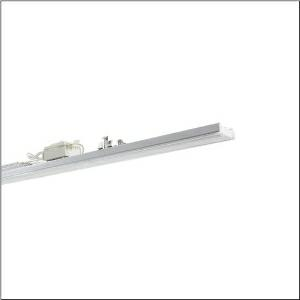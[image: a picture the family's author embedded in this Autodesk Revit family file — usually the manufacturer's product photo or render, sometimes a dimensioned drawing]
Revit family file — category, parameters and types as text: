
# Revit family: licross_r__11_recessed_ho_51tl1wdv4m2m_e1c2
name_source: partatom
category: Lighting Fixtures
units: mm (PartAtom-declared; Revit-internal decimal feet)

## family parameters
Cut with Voids When Loaded = No
Host = Face
Light Source = No
Part Type = Normal
Room Calculation Point = No
Round Connector Dimension = Use Diameter
Shared = No

## types (1)
- --- (1 x LED, 27420 lm, 150.5 W, 4000K)
    Apparent Load = 150 VA
    CIE Flux Codes = 73 94 99 100 100
    Color Rendering = 80
    Color Temperature = 4000K
    Default Elevation = 1800 mm
    Description = Licross® 11 Recessed HO, luminaire insert, of sheet steel, coil coated, white, length: 2.250mm, width: 66mm, height: 67mm, LED rated luminous flux: 27.420lm, light colour: 840, control gear: DALI 2, with plug, 5-pole, with phase selection, mains connection: 220..240V, AC, 50/60Hz, rated input power: 151W, internal wiring halogen-free, primary optical cover: cover, of PMMA, light emission: direct distribution, primary light characteristic: symmetric, protection rating (complete): IP40, insulation class (complete): insulation class I (protective earthing), certification: CE, ENEC, VDE, UKCA, protection symbol: D if used in an environment without relevant dust loads with corresponding accessories, impact resistance: IK06, permissible ambient temperature for indoor applications: -40..+35°C, corresponds to IFS (International Featured Standards) requirements for safety and quality in the food industry, reducing of maximum allowable ambient temperature of 5°C with ceiling mounting, LABS conformity tested according to VDMA 24364:2018-05, packaging unit: 1 piece
    Height = 58 mm
    Lamp = 1 x LED
    Lamp Light Flux = 27420 lm
    Lamp Power = 150.5 W
    Lamp count = 1
    Length = 2250 mm
    Luminous efficacy = 182 lm/W
    Manufacturer = Siteco
    ModVariant = No
    Model = 51TL1WDV4M2M
    Mounting Place = Ceiling
    Mounting Type = Pendant
    Number of Poles = 1
    OnlyDefault = Yes
    Power Factor = 1
    Product Name = Licross® 11 Recessed HO
    Product group = luminaire insert | ceiling pendant
    ProductGroupID = 902
    Protection Class = Protection class I
    Protection Degree = IP 40
    RLX_Detail_Level = 1
    RLX_Emergency_Light_Flux = 0 lm
    RLX_Emergency_Type = 0
    RLX_Emergency_Type_DB = No
    RlxData = <blob elided: 29653 chars, md5=4ee0cf90>
    Socket = socket
    Standby Power = 0 W
    System Light Flux = 27420 lm
    System Power = 150 W
    Type Comments = factory setting: luminous flux: 100 % | dim-lin: 254 | 690 mA
    Type Image = l_1296930.jpg
    URL = http://relux.com
    VarID = @adj_079435
    Voltage = 0 V
    Weight = 0.00 kg
    Width = 66 mm

## geometry (parser evidence)
native form markers: Blend x4, Sweep x9
no freeform markers — native parametric forms only
